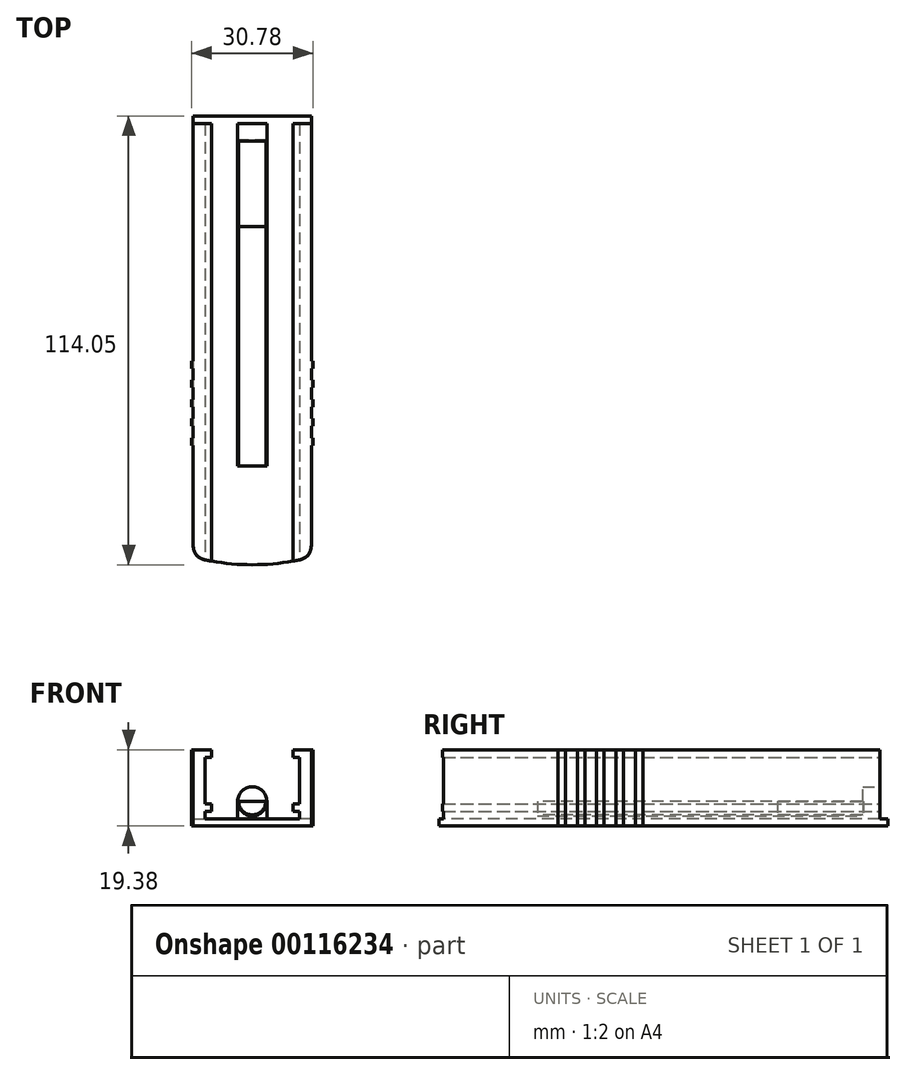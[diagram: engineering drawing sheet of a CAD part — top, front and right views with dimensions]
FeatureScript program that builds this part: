
annotation { "Feature Type Name" : "Feature", "Feature Type Description" : "" }
export const myFeature = defineFeature(function(context is Context, id is Id, definition is map)
    precondition{}
    {
        {
            var Q0;
            Q0=qCreatedBy(makeId("Top.planeOp"),FACE);
            var sketch = newSketch(context, id + "F0", { "sketchPlane" : qUnion([Q0])});
            skLineSegment(sketch, "E0.bottom", {"start": v(-15, 59) * mm, "end": v(15, 59) * mm});
            skLineSegment(sketch, "E0.top", {"start": v(-15, -59) * mm, "end": v(15, -59) * mm});
            skLineSegment(sketch, "E0.left", {"start": v(-15, 59) * mm, "end": v(-15, -59) * mm});
            skLineSegment(sketch, "E0.right", {"start": v(15, 59) * mm, "end": v(15, -59) * mm});
            skPoint(sketch, "E0.middle", {"position": v(0, 0) * mm});
            skLineSegment(sketch, "E1", {"start": v(-15, 57) * mm, "end": v(15, 57) * mm});
            skSolve(sketch);
        }
        {
            var Q0;
            Q0=qSketchRegion(id+"F0",true);
            extrude(context, id + "F1", {"entities" : qUnion([Q0]), "depth" : 1.78 * mm});
        }
        {
            var Q0;
            Q0=qCreatedBy(makeId("Top.planeOp"),FACE);
            var sketch = newSketch(context, id + "F2", { "sketchPlane" : qUnion([Q0])});
            skCircle(sketch, "E2", {"center": v(0, 3.76) * mm, "radius": 58.8 * mm});
            skSolve(sketch);
        }
        {
            var Q0;
            Q0=qSketchRegion(id+"F2",true);
            extrude(context, id + "F3", {"entities" : qUnion([Q0]), "operationType" : NewBodyOperationType.INTERSECT, "depth" : 6.98 * mm});
        }
        {
            var Q0;
            Q0=makeQuery(id+"F1.opExtrude","CAP_FACE",FACE,{"disambiguationData":[OSD([sQuery(id+"F0.wireOp",EDGE,"E0.bottom"),sQuery(id+"F0.wireOp",EDGE,"E0.top"),sQuery(id+"F0.wireOp",EDGE,"E0.left"),sQuery(id+"F0.wireOp",EDGE,"E0.right")])],"isStart":false});
            var sketch = newSketch(context, id + "F4", { "sketchPlane" : qUnion([Q0])});
            skSolve(sketch);
        }
        {
            var Q0;
            {var subQ0=sQuery(id+"F0.wireOp",EDGE,"E0.bottom");Q0=makeQuery(id+"F4.imprint","IMPRINT",FACE,{"disambiguationData":[TD([[makeQuery(id+"F4.imprint","IMPRINT",EDGE,{"derivedFrom":makeQuery(id+"F1.opExtrude","CAP_EDGE",EDGE,{"disambiguationData":[OSD([subQ0])],"isStart":false})}),-1.0]])]});}
            var sketch = newSketch(context, id + "F5", { "sketchPlane" : qUnion([Q0])});
            skLineSegment(sketch, "E3", {"start": v(0, 59) * mm, "end": v(0, -55.05) * mm});
            skSolve(sketch);
        }
        {
            var Q0;
            {var subQ4=sQuery(id+"F0.wireOp",EDGE,"E0.right");var subQ7=makeQuery(id+"F4.imprint","IMPRINT",EDGE,{"derivedFrom":makeQuery(id+"F1.opExtrude","CAP_EDGE",EDGE,{"disambiguationData":[OSD([subQ4])],"isStart":false})});Q0=makeQuery(id+"F5.imprint","IMPRINT",FACE,{"disambiguationData":[TD([[makeQuery(id+"F5.imprint","IMPRINT",EDGE,{"derivedFrom":subQ7}),-1.0]])]});}
            var Q1;
            Q1=sQuery(id+"F5.wireOp",EDGE,"E3");
            extrude(context, id + "F6", {"entities" : qUnion([Q0]), "operationType" : NewBodyOperationType.REMOVE, "surfaceEntities" : qUnion([Q1]), "oppositeDirection" : true, "depth" : 25 * mm});
        }
        {
            var Q0;
            Q0=makeQuery(id+"F1.opExtrude","CAP_FACE",FACE,{"disambiguationData":[OSD([sQuery(id+"F0.wireOp",EDGE,"E0.bottom"),sQuery(id+"F0.wireOp",EDGE,"E0.top"),sQuery(id+"F0.wireOp",EDGE,"E0.left"),sQuery(id+"F0.wireOp",EDGE,"E0.right")])],"isStart":false});
            var sketch = newSketch(context, id + "F7", { "sketchPlane" : qUnion([Q0])});
            skLineSegment(sketch, "E4", {"start": v(-15, 57) * mm, "end": v(0, 57) * mm});
            skLineSegment(sketch, "E5", {"start": v(-12, 57) * mm, "end": v(-12, -53.81) * mm});
            skSolve(sketch);
        }
        {
            var Q0;
            {var subQ4=sQuery(id+"F7.wireOp",EDGE,"E5");Q0=makeQuery(id+"F7.imprint","IMPRINT",FACE,{"disambiguationData":[TD([[makeQuery(id+"F7.imprint","IMPRINT",EDGE,{"derivedFrom":subQ4}),-1.0]])]});}
            extrude(context, id + "F8", {"entities" : qUnion([Q0]), "operationType" : NewBodyOperationType.ADD, "depth" : 17.6 * mm});
        }
        {
            var Q0;
            Q0=makeQuery(id+"F8.opExtrude","SWEPT_FACE",FACE,{"disambiguationData":[OSD([sQuery(id+"F7.wireOp",EDGE,"E4")])]});
            var sketch = newSketch(context, id + "F9", { "sketchPlane" : qUnion([Q0])});
            skLineSegment(sketch, "E6", {"start": v(12, 19.38) * mm, "end": v(10.4, 19.38) * mm});
            skLineSegment(sketch, "E7", {"start": v(10.4, 19.38) * mm, "end": v(10.4, 17.38) * mm});
            skLineSegment(sketch, "E8", {"start": v(10.4, 17.38) * mm, "end": v(12, 17.38) * mm});
            skLineSegment(sketch, "E9", {"start": v(12, 5.68) * mm, "end": v(10.4, 5.68) * mm});
            skLineSegment(sketch, "E10", {"start": v(10.4, 5.68) * mm, "end": v(10.4, 3.68) * mm});
            skLineSegment(sketch, "E11", {"start": v(10.4, 3.68) * mm, "end": v(12, 3.68) * mm});
            skSolve(sketch);
        }
        {
            var Q0;
            {var subQ0=sQuery(id+"F9.wireOp",EDGE,"E6");Q0=makeQuery(id+"F9.imprint","IMPRINT",FACE,{"disambiguationData":[TD([[makeQuery(id+"F9.imprint","IMPRINT",EDGE,{"derivedFrom":subQ0}),1.0]])]});}
            var Q1;
            {var subQ0=sQuery(id+"F9.wireOp",EDGE,"E9");Q1=makeQuery(id+"F9.imprint","IMPRINT",FACE,{"disambiguationData":[TD([[makeQuery(id+"F9.imprint","IMPRINT",EDGE,{"derivedFrom":subQ0}),1.0]])]});}
            var Q2;
            {var subQ0=sQuery(id+"F2.wireOp",EDGE,"E2");Q2=makeQuery(id+"F8.boolean.opBoolean","MERGE",FACE,{"derivedFrom":[makeQuery(id+"F3.boolean.opBoolean","COPY",FACE,{"derivedFrom":makeQuery(id+"F3.boolean.toolComplement.opBoolean","COPY",FACE,{"derivedFrom":makeQuery(id+"F3.opExtrude","SWEPT_FACE",FACE,{"disambiguationData":[OSD([subQ0])]})})}),makeQuery(id+"F8.opExtrude","SWEPT_FACE",FACE,{"disambiguationData":[OSD([sQuery(id+"F0.wireOp",EDGE,"E0.bottom"),sQuery(id+"F0.wireOp",EDGE,"E0.top"),sQuery(id+"F0.wireOp",EDGE,"E0.left"),sQuery(id+"F0.wireOp",EDGE,"E0.right"),subQ0])]})]});}
            extrude(context, id + "F10", {"entities" : qUnion([Q0, Q1]), "operationType" : NewBodyOperationType.ADD, "endBound" : BoundingType.UP_TO_SURFACE, "oppositeDirection" : true, "endBoundEntityFace" : qUnion([Q2]), "depth" : 25 * mm});
        }
        {
            var Q0;
            Q0=makeQuery(id+"F10.boolean.opBoolean","MERGE",FACE,{"derivedFrom":[makeQuery(id+"F8.opExtrude","CAP_FACE",FACE,{"disambiguationData":[OSD([sQuery(id+"F0.wireOp",EDGE,"E0.bottom"),sQuery(id+"F0.wireOp",EDGE,"E0.top"),sQuery(id+"F0.wireOp",EDGE,"E0.left"),sQuery(id+"F0.wireOp",EDGE,"E0.right"),sQuery(id+"F2.wireOp",EDGE,"E2"),sQuery(id+"F7.wireOp",EDGE,"E4"),sQuery(id+"F7.wireOp",EDGE,"E5")])],"isStart":false}),makeQuery(id+"F10.opExtrude","SWEPT_FACE",FACE,{"disambiguationData":[OSD([sQuery(id+"F9.wireOp",EDGE,"E6")])]})]});
            var sketch = newSketch(context, id + "F11", { "sketchPlane" : qUnion([Q0])});
            skLineSegment(sketch, "E12", {"start": v(-15, -3.25) * mm, "end": v(-15.39, -3.25) * mm});
            skLineSegment(sketch, "E13", {"start": v(-15.39, -3.25) * mm, "end": v(-15.39, -5.15) * mm});
            skLineSegment(sketch, "E14", {"start": v(-15.39, -5.15) * mm, "end": v(-15, -5.15) * mm});
            skLineSegment(sketch, "E15", {"start": v(-15, -8.15) * mm, "end": v(-15.39, -8.15) * mm});
            skLineSegment(sketch, "E16", {"start": v(-15.39, -8.15) * mm, "end": v(-15.39, -10.05) * mm});
            skLineSegment(sketch, "E17", {"start": v(-15.39, -10.05) * mm, "end": v(-15, -10.05) * mm});
            skLineSegment(sketch, "E18", {"start": v(-15, -13.05) * mm, "end": v(-15.39, -13.05) * mm});
            skLineSegment(sketch, "E19", {"start": v(-15.39, -13.05) * mm, "end": v(-15.39, -14.95) * mm});
            skLineSegment(sketch, "E20", {"start": v(-15.39, -14.95) * mm, "end": v(-15, -14.95) * mm});
            skLineSegment(sketch, "E21", {"start": v(-15, -17.95) * mm, "end": v(-15.39, -17.95) * mm});
            skLineSegment(sketch, "E22", {"start": v(-15.39, -17.95) * mm, "end": v(-15.39, -19.85) * mm});
            skLineSegment(sketch, "E23", {"start": v(-15.39, -19.85) * mm, "end": v(-15, -19.85) * mm});
            skLineSegment(sketch, "E24", {"start": v(-15, -22.85) * mm, "end": v(-15.39, -22.85) * mm});
            skLineSegment(sketch, "E25", {"start": v(-15.39, -22.85) * mm, "end": v(-15.39, -24.75) * mm});
            skLineSegment(sketch, "E26", {"start": v(-15.39, -24.75) * mm, "end": v(-15, -24.75) * mm});
            skSolve(sketch);
        }
        {
            var Q0;
            {var subQ0=sQuery(id+"F11.wireOp",EDGE,"E12");Q0=makeQuery(id+"F11.imprint","IMPRINT",FACE,{"disambiguationData":[TD([[makeQuery(id+"F11.imprint","IMPRINT",EDGE,{"derivedFrom":subQ0}),1.0]])]});}
            var Q1;
            {var subQ0=sQuery(id+"F11.wireOp",EDGE,"E15");Q1=makeQuery(id+"F11.imprint","IMPRINT",FACE,{"disambiguationData":[TD([[makeQuery(id+"F11.imprint","IMPRINT",EDGE,{"derivedFrom":subQ0}),1.0]])]});}
            var Q2;
            {var subQ0=sQuery(id+"F11.wireOp",EDGE,"E18");Q2=makeQuery(id+"F11.imprint","IMPRINT",FACE,{"disambiguationData":[TD([[makeQuery(id+"F11.imprint","IMPRINT",EDGE,{"derivedFrom":subQ0}),1.0]])]});}
            var Q3;
            {var subQ0=sQuery(id+"F11.wireOp",EDGE,"E21");Q3=makeQuery(id+"F11.imprint","IMPRINT",FACE,{"disambiguationData":[TD([[makeQuery(id+"F11.imprint","IMPRINT",EDGE,{"derivedFrom":subQ0}),1.0]])]});}
            var Q4;
            {var subQ0=sQuery(id+"F11.wireOp",EDGE,"E24");Q4=makeQuery(id+"F11.imprint","IMPRINT",FACE,{"disambiguationData":[TD([[makeQuery(id+"F11.imprint","IMPRINT",EDGE,{"derivedFrom":subQ0}),1.0]])]});}
            extrude(context, id + "F12", {"entities" : qUnion([Q0, Q1, Q2, Q3, Q4]), "operationType" : NewBodyOperationType.ADD, "oppositeDirection" : true, "depth" : 19.35 * mm});
        }
        {
            var Q0;
            {var subQ0=sQuery(id+"F2.wireOp",EDGE,"E2");var subQ1=sQuery(id+"F0.wireOp",EDGE,"E0.left");Q0=makeQuery(id+"F8.boolean.opBoolean","MERGE",EDGE,{"derivedFrom":[makeQuery(id+"F3.boolean.opBoolean","INTERSECT",EDGE,{"derivedFrom":[makeQuery(id+"F1.opExtrude","SWEPT_FACE",FACE,{"disambiguationData":[OSD([subQ1])]}),makeQuery(id+"F3.boolean.toolComplement.opBoolean","COPY",FACE,{"derivedFrom":makeQuery(id+"F3.opExtrude","SWEPT_FACE",FACE,{"disambiguationData":[OSD([subQ0])]})})]}),makeQuery(id+"F8.opExtrude","SWEPT_EDGE",EDGE,{"disambiguationData":[OSD([sQuery(id+"F0.wireOp",EDGE,"E0.bottom"),sQuery(id+"F0.wireOp",EDGE,"E0.top"),subQ1,sQuery(id+"F0.wireOp",EDGE,"E0.right"),subQ0])]})]});}
            fillet(context, id + "F13", {"entities" : qUnion([Q0]), "radius" : 4 * mm, "tangentPropagation" : true, "rho" : 0.5, "crossSection" : FilletCrossSection.CONIC, "allowEdgeOverflow" : false});
        }
        {
            var Q0;
            Q0=makeQuery(id+"F1.opExtrude","CAP_FACE",FACE,{"disambiguationData":[OSD([sQuery(id+"F0.wireOp",EDGE,"E0.bottom"),sQuery(id+"F0.wireOp",EDGE,"E0.top"),sQuery(id+"F0.wireOp",EDGE,"E0.left"),sQuery(id+"F0.wireOp",EDGE,"E0.right")])],"isStart":false});
            var sketch = newSketch(context, id + "F14", { "sketchPlane" : qUnion([Q0])});
            skLineSegment(sketch, "E27", {"start": v(-15, 57) * mm, "end": v(0, 57) * mm});
            skLineSegment(sketch, "E28", {"start": v(-3.7, 57) * mm, "end": v(-3.7, 52.88) * mm});
            skLineSegment(sketch, "E29", {"start": v(-3.7, 52.88) * mm, "end": v(0, 52.88) * mm});
            skSolve(sketch);
        }
        {
            var Q0;
            {var subQ3=sQuery(id+"F14.wireOp",EDGE,"E28");Q0=makeQuery(id+"F14.imprint","IMPRINT",FACE,{"disambiguationData":[TD([[makeQuery(id+"F14.imprint","IMPRINT",EDGE,{"derivedFrom":subQ3}),1.0]])]});}
            extrude(context, id + "F15", {"entities" : qUnion([Q0]), "operationType" : NewBodyOperationType.ADD, "depth" : 4.5 * mm});
        }
        {
            var Q0;
            Q0=makeQuery(id+"F1.opExtrude","SWEPT_BODY",BODY,{"disambiguationData":[OSD([sQuery(id+"F0.wireOp",EDGE,"E0.bottom"),sQuery(id+"F0.wireOp",EDGE,"E0.top"),sQuery(id+"F0.wireOp",EDGE,"E0.left"),sQuery(id+"F0.wireOp",EDGE,"E0.right")])]});
            var Q1;
            Q1=qCreatedBy(makeId("Right.planeOp"),FACE);
            mirror(context, id + "F16", {"operationType" : NewBodyOperationType.ADD, "entities" : qUnion([Q0]), "mirrorPlane" : qUnion([Q1])});
        }
        {
            var Q0;
            {var subQ0=makeQuery(id+"F15.opExtrude","SWEPT_FACE",FACE,{"disambiguationData":[OSD([sQuery(id+"F14.wireOp",EDGE,"E27")])]});Q0=makeQuery(id+"F16.boolean.opBoolean","MERGE",FACE,{"derivedFrom":[subQ0,makeQuery(id+"F16.opPattern","COPY",FACE,{"derivedFrom":subQ0,"instanceName":"1"})]});}
            var sketch = newSketch(context, id + "F17", { "sketchPlane" : qUnion([Q0])});
            skCircle(sketch, "E30", {"center": v(0, 6.28) * mm, "radius": 3.7 * mm});
            skSolve(sketch);
        }
        {
            var Q0;
            {var subQ1=sQuery(id+"F14.wireOp",EDGE,"E27");var subQ2=makeQuery(id+"F15.opExtrude","CAP_EDGE",EDGE,{"disambiguationData":[OSD([subQ1])],"isStart":false});var subQ3=makeQuery(id+"F16.boolean.opBoolean","MERGE",EDGE,{"derivedFrom":[subQ2,makeQuery(id+"F16.opPattern","COPY",EDGE,{"derivedFrom":subQ2,"instanceName":"1"})]});Q0=makeQuery(id+"F17.imprint","IMPRINT",FACE,{"disambiguationData":[TD([[makeQuery(id+"F17.imprint","IMPRINT",EDGE,{"derivedFrom":subQ3}),-1.0]])]});}
            var Q1;
            Q1=qSketchRegion(id+"F17",true);
            extrude(context, id + "F18", {"entities" : qUnion([Q0, Q1]), "operationType" : NewBodyOperationType.ADD, "oppositeDirection" : true, "depth" : 87 * mm});
        }
        {
            var Q0;
            Q0=makeQuery(id+"F18.opExtrude","CAP_FACE",FACE,{"disambiguationData":[OSD([sQuery(id+"F17.wireOp",EDGE,"E30")])],"isStart":false});
            var sketch = newSketch(context, id + "F19", { "sketchPlane" : qUnion([Q0])});
            skCircle(sketch, "E31", {"center": v(0, 6.28) * mm, "radius": 3.46 * mm});
            skLineSegment(sketch, "E32", {"start": v(-3.7, 6.28) * mm, "end": v(3.7, 6.28) * mm});
            skSolve(sketch);
        }
        {
            var Q0;
            {var subQ0=sQuery(id+"F19.wireOp",EDGE,"E32");var subQ1=sQuery(id+"F19.wireOp",EDGE,"E31");var subQ2=makeQuery(id+"F19.imprint","INTERSECT",VERTEX,{"disambiguationData":[OD(0.0)],"derivedFrom":[subQ1,subQ0]});Q0=makeQuery(id+"F19.imprint","IMPRINT",FACE,{"disambiguationData":[TD([[makeQuery(id+"F19.imprint","IMPRINT",EDGE,{"disambiguationData":[TD([[subQ2,1.0]])],"derivedFrom":subQ1}),1.0]])]});}
            var Q1;
            {var subQ0=sQuery(id+"F19.wireOp",EDGE,"E32");var subQ1=sQuery(id+"F19.wireOp",EDGE,"E31");var subQ2=makeQuery(id+"F19.imprint","INTERSECT",VERTEX,{"disambiguationData":[OD(0.0)],"derivedFrom":[subQ1,subQ0]});Q1=makeQuery(id+"F19.imprint","IMPRINT",FACE,{"disambiguationData":[TD([[makeQuery(id+"F19.imprint","IMPRINT",EDGE,{"disambiguationData":[TD([[subQ2,1.0]])],"derivedFrom":subQ1}),-1.0]])]});}
            var Q2;
            {var subQ0=sQuery(id+"F19.wireOp",EDGE,"E32");var subQ1=sQuery(id+"F19.wireOp",EDGE,"E31");var subQ2=makeQuery(id+"F19.imprint","INTERSECT",VERTEX,{"disambiguationData":[OD(0.0)],"derivedFrom":[subQ1,subQ0]});Q2=makeQuery(id+"F19.imprint","IMPRINT",FACE,{"disambiguationData":[TD([[makeQuery(id+"F19.imprint","IMPRINT",EDGE,{"disambiguationData":[TD([[subQ2,-1.0]])],"derivedFrom":subQ1}),1.0]])]});}
            extrude(context, id + "F20", {"entities" : qUnion([Q0, Q1, Q2]), "operationType" : NewBodyOperationType.REMOVE, "oppositeDirection" : true, "depth" : 82.64 * mm});
        }
        {
            var Q0;
            Q0=makeQuery(id+"F20.boolean.opBoolean","COPY",FACE,{"derivedFrom":makeQuery(id+"F20.opExtrude","CAP_FACE",FACE,{"disambiguationData":[OSD([sQuery(id+"F17.wireOp",EDGE,"E30"),sQuery(id+"F19.wireOp",EDGE,"E31"),sQuery(id+"F19.wireOp",EDGE,"E32")])],"isStart":false})});
            var sketch = newSketch(context, id + "F21", { "sketchPlane" : qUnion([Q0])});
            skArc(sketch, "E33", {"start": v(-3.46, 6.28) * mm, "mid": v(0, 2.82) * mm, "end": v(3.46, 6.28) * mm});
            skLineSegment(sketch, "E34", {"start": v(-3.46, 6.28) * mm, "end": v(3.46, 6.28) * mm});
            skSolve(sketch);
        }
        {
            var Q0;
            Q0=makeQuery(id+"F21.imprint","IMPRINT",FACE,{"disambiguationData":[TD([[makeQuery(id+"F21.imprint","IMPRINT",EDGE,{"derivedFrom":sQuery(id+"F21.wireOp",EDGE,"E33")}),1.0]])]});
            extrude(context, id + "F22", {"entities" : qUnion([Q0]), "depth" : 21.7 * mm});
        }
    });
